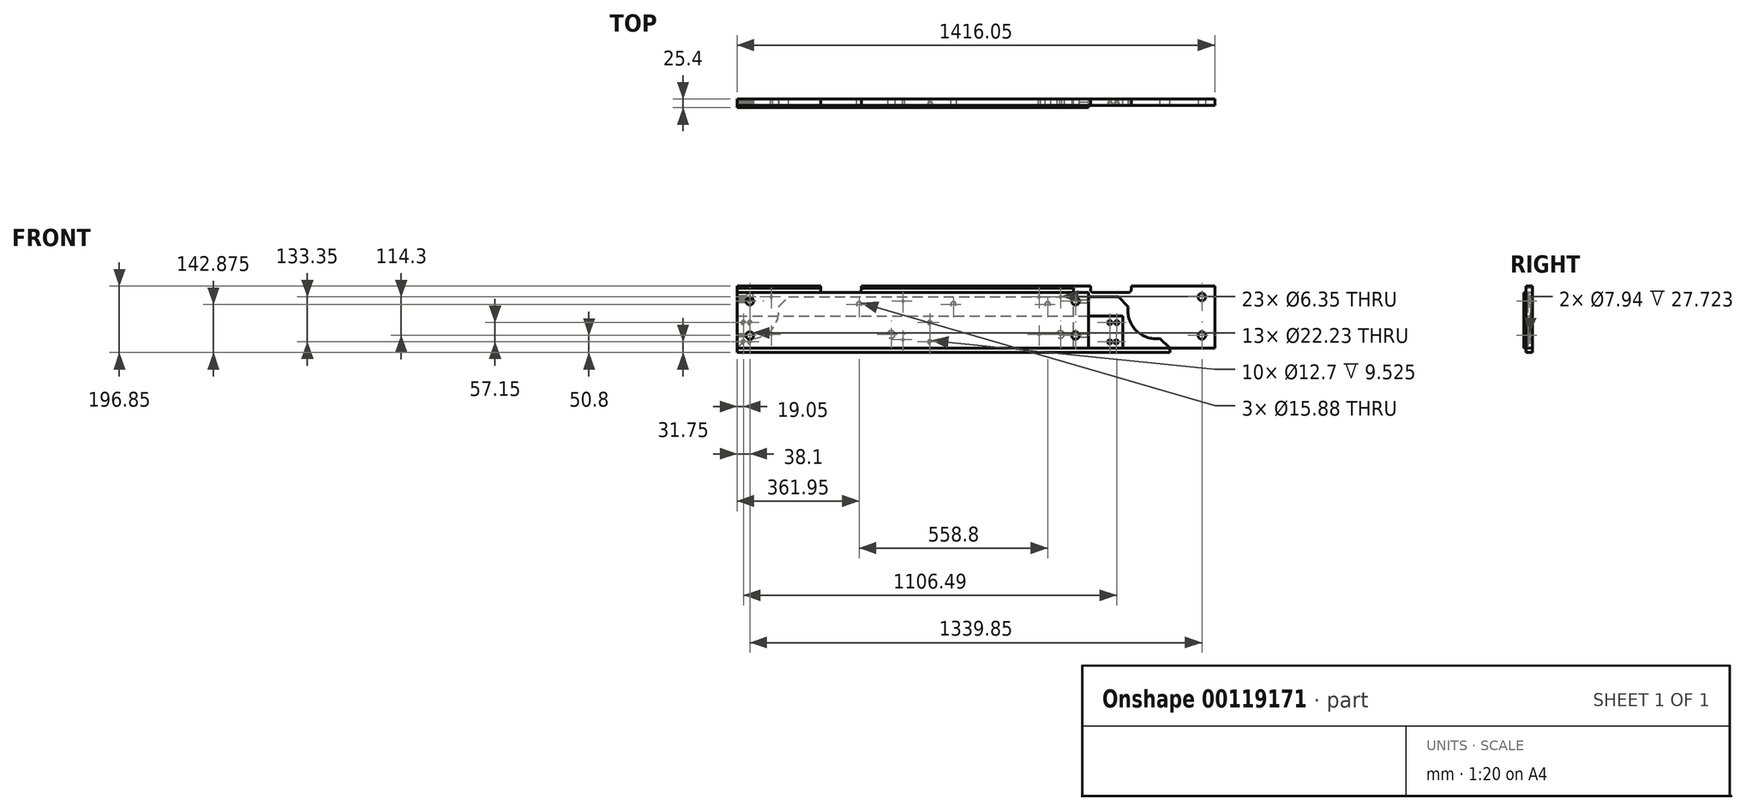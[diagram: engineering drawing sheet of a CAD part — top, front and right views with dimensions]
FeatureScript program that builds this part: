
annotation { "Feature Type Name" : "Feature", "Feature Type Description" : "" }
export const myFeature = defineFeature(function(context is Context, id is Id, definition is map)
    precondition{}
    {
        {
            var Q0;
            Q0=qCreatedBy(makeId("Front.planeOp"),FACE);
            var sketch = newSketch(context, id + "F30", { "sketchPlane" : qUnion([Q0])});
            skLineSegment(sketch, "E0.bottom", {"start": v(0, -12.7) * mm, "end": v(1282.7, -12.7) * mm});
            skLineSegment(sketch, "E0.top", {"start": v(152.4, 152.4) * mm, "end": v(1130.3, 152.4) * mm});
            skLineSegment(sketch, "E0.left", {"start": v(0, 0) * mm, "end": v(152.4, 152.4) * mm});
            skLineSegment(sketch, "E0.right", {"start": v(1282.7, 0) * mm, "end": v(1130.3, 152.4) * mm});
            skLineSegment(sketch, "E1", {"start": v(0, -12.7) * mm, "end": v(0, 0) * mm});
            skLineSegment(sketch, "E2", {"start": v(1282.7, -12.7) * mm, "end": v(1282.7, 0) * mm});
            skSolve(sketch);
        }
        {
            var Q0;
            Q0=makeQuery(id+"F30.imprint","IMPRINT",FACE,{"disambiguationData":[TD([[makeQuery(id+"F30.imprint","IMPRINT",EDGE,{"derivedFrom":sQuery(id+"F30.wireOp",EDGE,"E0.bottom")}),1.0]])]});
            extrude(context, id + "F31", {"entities" : qUnion([Q0]), "depth" : 19.05 * mm});
        }
        {
            var Q0;
            Q0=makeQuery(id+"F31.opExtrude","CAP_FACE",FACE,{"disambiguationData":[OSD([sQuery(id+"F30.wireOp",EDGE,"E0.bottom"),sQuery(id+"F30.wireOp",EDGE,"E0.top"),sQuery(id+"F30.wireOp",EDGE,"E0.left"),sQuery(id+"F30.wireOp",EDGE,"E0.right"),sQuery(id+"F30.wireOp",EDGE,"E1"),sQuery(id+"F30.wireOp",EDGE,"E2")])],"isStart":false});
            var sketch = newSketch(context, id + "F0", { "sketchPlane" : qUnion([Q0])});
            skCircle(sketch, "E3", {"center": v(1241.43, 111.13) * mm, "radius": 82.55 * mm});
            skCircle(sketch, "E4", {"center": v(41.28, 111.13) * mm, "radius": 82.55 * mm});
            skSolve(sketch);
        }
        {
            var Q0;
            {var subQ0=sQuery(id+"F0.wireOp",EDGE,"E4");var subQ1=makeQuery(id+"F31.opExtrude","CAP_EDGE",EDGE,{"disambiguationData":[OSD([sQuery(id+"F30.wireOp",EDGE,"E0.left")])],"isStart":false});var subQ2=makeQuery(id+"F0.imprint","INTERSECT",VERTEX,{"disambiguationData":[OD(0.0)],"derivedFrom":[subQ1,subQ0]});Q0=makeQuery(id+"F0.imprint","IMPRINT",FACE,{"disambiguationData":[TD([[makeQuery(id+"F0.imprint","IMPRINT",EDGE,{"disambiguationData":[TD([[subQ2,-1.0]])],"derivedFrom":subQ0}),1.0]])]});}
            var Q1;
            {var subQ0=sQuery(id+"F0.wireOp",EDGE,"E4");var subQ1=makeQuery(id+"F31.opExtrude","CAP_EDGE",EDGE,{"disambiguationData":[OSD([sQuery(id+"F30.wireOp",EDGE,"E0.left")])],"isStart":false});var subQ2=makeQuery(id+"F0.imprint","INTERSECT",VERTEX,{"disambiguationData":[OD(0.0)],"derivedFrom":[subQ1,subQ0]});Q1=makeQuery(id+"F0.imprint","IMPRINT",FACE,{"disambiguationData":[TD([[makeQuery(id+"F0.imprint","IMPRINT",EDGE,{"disambiguationData":[TD([[subQ2,1.0]])],"derivedFrom":subQ0}),1.0]])]});}
            var Q2;
            {var subQ0=sQuery(id+"F0.wireOp",EDGE,"E3");var subQ1=makeQuery(id+"F31.opExtrude","CAP_EDGE",EDGE,{"disambiguationData":[OSD([sQuery(id+"F30.wireOp",EDGE,"E0.right")])],"isStart":false});var subQ2=makeQuery(id+"F0.imprint","INTERSECT",VERTEX,{"disambiguationData":[OD(0.0)],"derivedFrom":[subQ1,subQ0]});Q2=makeQuery(id+"F0.imprint","IMPRINT",FACE,{"disambiguationData":[TD([[makeQuery(id+"F0.imprint","IMPRINT",EDGE,{"disambiguationData":[TD([[subQ2,1.0]])],"derivedFrom":subQ0}),1.0]])]});}
            var Q3;
            {var subQ0=sQuery(id+"F0.wireOp",EDGE,"E3");var subQ1=makeQuery(id+"F31.opExtrude","CAP_EDGE",EDGE,{"disambiguationData":[OSD([sQuery(id+"F30.wireOp",EDGE,"E0.right")])],"isStart":false});var subQ2=makeQuery(id+"F0.imprint","INTERSECT",VERTEX,{"disambiguationData":[OD(0.0)],"derivedFrom":[subQ1,subQ0]});Q3=makeQuery(id+"F0.imprint","IMPRINT",FACE,{"disambiguationData":[TD([[makeQuery(id+"F0.imprint","IMPRINT",EDGE,{"disambiguationData":[TD([[subQ2,-1.0]])],"derivedFrom":subQ0}),1.0]])]});}
            extrude(context, id + "F1", {"entities" : qUnion([Q0, Q1, Q2, Q3]), "operationType" : NewBodyOperationType.REMOVE, "oppositeDirection" : true, "depth" : 25.4 * mm});
        }
        {
            var Q0;
            Q0=makeQuery(id+"F31.opExtrude","CAP_FACE",FACE,{"disambiguationData":[OSD([sQuery(id+"F30.wireOp",EDGE,"E0.bottom"),sQuery(id+"F30.wireOp",EDGE,"E0.top"),sQuery(id+"F30.wireOp",EDGE,"E0.left"),sQuery(id+"F30.wireOp",EDGE,"E0.right"),sQuery(id+"F30.wireOp",EDGE,"E1"),sQuery(id+"F30.wireOp",EDGE,"E2")])],"isStart":false});
            var sketch = newSketch(context, id + "F2", { "sketchPlane" : qUnion([Q0])});
            skCircle(sketch, "E5", {"center": v(361.95, 130.18) * mm, "radius": 7.94 * mm});
            skCircle(sketch, "E6", {"center": v(641.35, 130.18) * mm, "radius": 7.94 * mm});
            skCircle(sketch, "E7", {"center": v(920.75, 130.18) * mm, "radius": 7.94 * mm});
            skSolve(sketch);
        }
        {
            var Q0;
            Q0 = qSketchRegion(id + "F2", true);
            extrude(context, id + "F3", {"entities" : qUnion([Q0]), "operationType" : NewBodyOperationType.REMOVE, "oppositeDirection" : true, "depth" : 50.8 * mm});
        }
        {
            var Q0;
            Q0=qCreatedBy(makeId("Front.planeOp"),FACE);
            var sketch = newSketch(context, id + "F4", { "sketchPlane" : qUnion([Q0])});
            skLineSegment(sketch, "E8.bottom", {"start": v(0, 0) * mm, "end": v(996.95, 0) * mm});
            skLineSegment(sketch, "E8.top", {"start": v(0, 177.8) * mm, "end": v(996.95, 177.8) * mm});
            skLineSegment(sketch, "E8.left", {"start": v(0, 0) * mm, "end": v(0, 177.8) * mm});
            skLineSegment(sketch, "E8.right", {"start": v(996.95, 0) * mm, "end": v(996.95, 177.8) * mm});
            skSolve(sketch);
        }
        {
            var Q0;
            Q0=makeQuery(id+"F4.imprint","IMPRINT",FACE,{"disambiguationData":[TD([[makeQuery(id+"F4.imprint","IMPRINT",EDGE,{"derivedFrom":sQuery(id+"F4.wireOp",EDGE,"E8.bottom")}),1.0]])]});
            extrude(context, id + "F5", {"entities" : qUnion([Q0]), "depth" : 19.05 * mm});
        }
        {
            var Q0;
            Q0=makeQuery(id+"F5.opExtrude","CAP_FACE",FACE,{"disambiguationData":[OSD([sQuery(id+"F4.wireOp",EDGE,"E8.bottom"),sQuery(id+"F4.wireOp",EDGE,"E8.top"),sQuery(id+"F4.wireOp",EDGE,"E8.left"),sQuery(id+"F4.wireOp",EDGE,"E8.right")])],"isStart":false});
            var sketch = newSketch(context, id + "F6", { "sketchPlane" : qUnion([Q0])});
            skCircle(sketch, "E9", {"center": v(958.85, 152.4) * mm, "radius": 3.18 * mm});
            skCircle(sketch, "E10", {"center": v(958.85, 41.27) * mm, "radius": 3.18 * mm});
            skCircle(sketch, "E11", {"center": v(492.13, 139.7) * mm, "radius": 3.18 * mm});
            skCircle(sketch, "E12", {"center": v(492.13, 25.4) * mm, "radius": 3.18 * mm});
            skCircle(sketch, "E13", {"center": v(38.1, 152.4) * mm, "radius": 3.18 * mm});
            skCircle(sketch, "E14", {"center": v(38.1, 41.27) * mm, "radius": 3.18 * mm});
            skCircle(sketch, "E15", {"center": v(101.6, 152.4) * mm, "radius": 3.18 * mm});
            skCircle(sketch, "E16", {"center": v(101.6, 41.27) * mm, "radius": 3.18 * mm});
            skCircle(sketch, "E17", {"center": v(895.35, 152.4) * mm, "radius": 3.18 * mm});
            skCircle(sketch, "E18", {"center": v(895.35, 41.27) * mm, "radius": 3.18 * mm});
            skSolve(sketch);
        }
        {
            var Q0;
            Q0 = qSketchRegion(id + "F6", true);
            extrude(context, id + "F7", {"entities" : qUnion([Q0]), "operationType" : NewBodyOperationType.REMOVE, "oppositeDirection" : true, "depth" : 25.4 * mm});
        }
        {
            var Q0;
            Q0=qCreatedBy(makeId("Front.planeOp"),FACE);
            var sketch = newSketch(context, id + "F8", { "sketchPlane" : qUnion([Q0])});
            skLineSegment(sketch, "E19.bottom", {"start": v(0, 0) * mm, "end": v(1041.4, 0) * mm});
            skLineSegment(sketch, "E19.top", {"start": v(0, 165.1) * mm, "end": v(1041.4, 165.1) * mm});
            skLineSegment(sketch, "E19.left", {"start": v(0, 0) * mm, "end": v(0, 165.1) * mm});
            skLineSegment(sketch, "E19.right", {"start": v(1041.4, 0) * mm, "end": v(1041.4, 165.1) * mm});
            skSolve(sketch);
        }
        {
            var Q0;
            Q0=makeQuery(id+"F8.imprint","IMPRINT",FACE,{"disambiguationData":[TD([[makeQuery(id+"F8.imprint","IMPRINT",EDGE,{"derivedFrom":sQuery(id+"F8.wireOp",EDGE,"E19.bottom")}),1.0]])]});
            extrude(context, id + "F9", {"entities" : qUnion([Q0]), "depth" : 25.4 * mm});
        }
        {
            var Q0;
            Q0=makeQuery(id+"F9.opExtrude","CAP_FACE",FACE,{"disambiguationData":[OSD([sQuery(id+"F8.wireOp",EDGE,"E19.bottom"),sQuery(id+"F8.wireOp",EDGE,"E19.top"),sQuery(id+"F8.wireOp",EDGE,"E19.left"),sQuery(id+"F8.wireOp",EDGE,"E19.right")])],"isStart":false});
            var sketch = newSketch(context, id + "F10", { "sketchPlane" : qUnion([Q0])});
            skCircle(sketch, "E20", {"center": v(1003.3, 139.7) * mm, "radius": 11.11 * mm});
            skCircle(sketch, "E21", {"center": v(1003.3, 38.1) * mm, "radius": 11.11 * mm});
            skSolve(sketch);
        }
        {
            var Q0;
            Q0 = qSketchRegion(id + "F10", true);
            extrude(context, id + "F11", {"entities" : qUnion([Q0]), "operationType" : NewBodyOperationType.REMOVE, "oppositeDirection" : true, "depth" : 25.4 * mm});
        }
        {
            var Q0;
            Q0=makeQuery(id+"F9.opExtrude","SWEPT_FACE",FACE,{"disambiguationData":[OSD([sQuery(id+"F8.wireOp",EDGE,"E19.right")])]});
            var sketch = newSketch(context, id + "F12", { "sketchPlane" : qUnion([Q0])});
            skCircle(sketch, "E22", {"center": v(-12.7, 38.1) * mm, "radius": 3.97 * mm});
            skCircle(sketch, "E23", {"center": v(-12.7, 139.7) * mm, "radius": 3.97 * mm});
            skSolve(sketch);
        }
        {
            var Q0;
            Q0 = qSketchRegion(id + "F12", true);
            extrude(context, id + "F13", {"entities" : qUnion([Q0]), "operationType" : NewBodyOperationType.REMOVE, "oppositeDirection" : true, "depth" : 38.1 * mm});
        }
        {
            var Q0;
            Q0=makeQuery(id+"F9.opExtrude","CAP_FACE",FACE,{"disambiguationData":[OSD([sQuery(id+"F8.wireOp",EDGE,"E19.bottom"),sQuery(id+"F8.wireOp",EDGE,"E19.top"),sQuery(id+"F8.wireOp",EDGE,"E19.left"),sQuery(id+"F8.wireOp",EDGE,"E19.right")])],"isStart":false});
            var sketch = newSketch(context, id + "F14", { "sketchPlane" : qUnion([Q0])});
            skCircle(sketch, "E24", {"center": v(38.1, 139.7) * mm, "radius": 11.11 * mm});
            skCircle(sketch, "E25", {"center": v(38.1, 38.1) * mm, "radius": 11.11 * mm});
            skSolve(sketch);
        }
        {
            var Q0;
            Q0 = qSketchRegion(id + "F14", true);
            extrude(context, id + "F15", {"entities" : qUnion([Q0]), "operationType" : NewBodyOperationType.REMOVE, "oppositeDirection" : true, "depth" : 25.4 * mm});
        }
        {
            var Q0;
            Q0=makeQuery(id+"F9.opExtrude","SWEPT_FACE",FACE,{"disambiguationData":[OSD([sQuery(id+"F8.wireOp",EDGE,"E19.left")])]});
            var sketch = newSketch(context, id + "F16", { "sketchPlane" : qUnion([Q0])});
            skCircle(sketch, "E26", {"center": v(12.7, 139.7) * mm, "radius": 3.97 * mm});
            skCircle(sketch, "E27", {"center": v(12.7, 38.1) * mm, "radius": 3.97 * mm});
            skSolve(sketch);
        }
        {
            var Q0;
            Q0 = qSketchRegion(id + "F16", true);
            extrude(context, id + "F17", {"entities" : qUnion([Q0]), "operationType" : NewBodyOperationType.REMOVE, "oppositeDirection" : true, "depth" : 38.1 * mm});
        }
        {
            var Q0;
            Q0=qCreatedBy(makeId("Front.planeOp"),FACE);
            var sketch = newSketch(context, id + "F18", { "sketchPlane" : qUnion([Q0])});
            skLineSegment(sketch, "E28.bottom", {"start": v(0, 0) * mm, "end": v(1143, 0) * mm});
            skLineSegment(sketch, "E28.top", {"start": v(0, 95.25) * mm, "end": v(1143, 95.25) * mm});
            skLineSegment(sketch, "E28.left", {"start": v(0, 0) * mm, "end": v(0, 95.25) * mm});
            skLineSegment(sketch, "E28.right", {"start": v(1143, 0) * mm, "end": v(1143, 95.25) * mm});
            skSolve(sketch);
        }
        {
            var Q0;
            Q0=makeQuery(id+"F18.imprint","IMPRINT",FACE,{"disambiguationData":[TD([[makeQuery(id+"F18.imprint","IMPRINT",EDGE,{"derivedFrom":sQuery(id+"F18.wireOp",EDGE,"E28.bottom")}),1.0]])]});
            extrude(context, id + "F19", {"entities" : qUnion([Q0]), "depth" : 19.05 * mm});
        }
        {
            var Q0;
            Q0=makeQuery(id+"F19.opExtrude","CAP_FACE",FACE,{"disambiguationData":[OSD([sQuery(id+"F18.wireOp",EDGE,"E28.bottom"),sQuery(id+"F18.wireOp",EDGE,"E28.top"),sQuery(id+"F18.wireOp",EDGE,"E28.left"),sQuery(id+"F18.wireOp",EDGE,"E28.right")])],"isStart":false});
            var sketch = newSketch(context, id + "F20", { "sketchPlane" : qUnion([Q0])});
            skPoint(sketch, "E29", {"position": v(19.05, 76.2) * mm});
            skPoint(sketch, "E30", {"position": v(38.1, 76.2) * mm});
            skPoint(sketch, "E31", {"position": v(19.05, 19.05) * mm});
            skPoint(sketch, "E32", {"position": v(38.1, 19.05) * mm});
            skPoint(sketch, "E33", {"position": v(571.5, 76.2) * mm});
            skPoint(sketch, "E34", {"position": v(571.5, 19.05) * mm});
            skPoint(sketch, "E35", {"position": v(1104.9, 19.05) * mm});
            skPoint(sketch, "E36", {"position": v(1123.95, 19.05) * mm});
            skPoint(sketch, "E37", {"position": v(1125.54, 76.2) * mm});
            skPoint(sketch, "E38", {"position": v(1104.9, 76.2) * mm});
            skSolve(sketch);
        }
        {
            var Q0;
            Q0=sQuery(id+"F20.wireOp",VERTEX,"E29");
            var Q1;
            Q1=sQuery(id+"F20.wireOp",VERTEX,"E30");
            var Q2;
            Q2=sQuery(id+"F20.wireOp",VERTEX,"E31");
            var Q3;
            Q3=sQuery(id+"F20.wireOp",VERTEX,"E32");
            var Q4;
            Q4=sQuery(id+"F20.wireOp",VERTEX,"E33");
            var Q5;
            Q5=sQuery(id+"F20.wireOp",VERTEX,"E34");
            var Q6;
            Q6=sQuery(id+"F20.wireOp",VERTEX,"E38");
            var Q7;
            Q7=sQuery(id+"F20.wireOp",VERTEX,"E37");
            var Q8;
            Q8=sQuery(id+"F20.wireOp",VERTEX,"E35");
            var Q9;
            Q9=sQuery(id+"F20.wireOp",VERTEX,"E36");
            var Q10;
            Q10=makeQuery(id+"F19.opExtrude","SWEPT_BODY",BODY,{"disambiguationData":[OSD([sQuery(id+"F18.wireOp",EDGE,"E28.bottom"),sQuery(id+"F18.wireOp",EDGE,"E28.top"),sQuery(id+"F18.wireOp",EDGE,"E28.left"),sQuery(id+"F18.wireOp",EDGE,"E28.right")])]});
            hole(context, id + "F21", {"style" : HoleStyle.C_BORE, "endStyle" : HoleEndStyle.THROUGH, "holeDiameter" : 6.35 * mm, "cBoreDiameter" : 12.7 * mm, "cBoreDepth" : 9.52 * mm, "isTappedThrough" : true, "tappedDepth" : 12.7 * mm, "tapClearance" : 3, "locations" : qUnion([Q0, Q1, Q2, Q3, Q4, Q5, Q6, Q7, Q8, Q9]), "scope" : qUnion([Q10])});
        }
        {
            var Q0;
            Q0=qCreatedBy(makeId("Front.planeOp"),FACE);
            var sketch = newSketch(context, id + "F22", { "sketchPlane" : qUnion([Q0])});
            skLineSegment(sketch, "E39.bottom", {"start": v(0, 0) * mm, "end": v(1416.05, 0) * mm});
            skLineSegment(sketch, "E39.top", {"start": v(0, 184.15) * mm, "end": v(1416.05, 184.15) * mm});
            skLineSegment(sketch, "E39.left", {"start": v(0, 0) * mm, "end": v(0, 184.15) * mm});
            skLineSegment(sketch, "E39.right", {"start": v(1416.05, 0) * mm, "end": v(1416.05, 184.15) * mm});
            skSolve(sketch);
        }
        {
            var Q0;
            Q0=makeQuery(id+"F22.imprint","IMPRINT",FACE,{"disambiguationData":[TD([[makeQuery(id+"F22.imprint","IMPRINT",EDGE,{"derivedFrom":sQuery(id+"F22.wireOp",EDGE,"E39.bottom")}),1.0]])]});
            extrude(context, id + "F23", {"entities" : qUnion([Q0]), "depth" : 19.05 * mm});
        }
        {
            var Q0;
            Q0=makeQuery(id+"F23.opExtrude","CAP_FACE",FACE,{"disambiguationData":[OSD([sQuery(id+"F22.wireOp",EDGE,"E39.bottom"),sQuery(id+"F22.wireOp",EDGE,"E39.top"),sQuery(id+"F22.wireOp",EDGE,"E39.left"),sQuery(id+"F22.wireOp",EDGE,"E39.right")])],"isStart":false});
            var sketch = newSketch(context, id + "F24", { "sketchPlane" : qUnion([Q0])});
            skPoint(sketch, "E40", {"position": v(38.1, 38.1) * mm});
            skPoint(sketch, "E41", {"position": v(38.1, 152.4) * mm});
            skPoint(sketch, "E42", {"position": v(1377.95, 152.4) * mm});
            skPoint(sketch, "E43", {"position": v(1377.95, 38.1) * mm});
            skPoint(sketch, "E44", {"position": v(958.85, 41.28) * mm});
            skPoint(sketch, "E45", {"position": v(457.2, 41.28) * mm});
            skLineSegment(sketch, "E46.bottom", {"start": v(247.65, 184.15) * mm, "end": v(368.3, 184.15) * mm});
            skLineSegment(sketch, "E46.top", {"start": v(247.65, 165.1) * mm, "end": v(368.3, 165.1) * mm});
            skLineSegment(sketch, "E46.left", {"start": v(247.65, 184.15) * mm, "end": v(247.65, 165.1) * mm});
            skLineSegment(sketch, "E46.right", {"start": v(368.3, 184.15) * mm, "end": v(368.3, 165.1) * mm});
            skLineSegment(sketch, "E47.bottom", {"start": v(1047.75, 184.15) * mm, "end": v(1168.4, 184.15) * mm});
            skLineSegment(sketch, "E47.top", {"start": v(1047.75, 165.1) * mm, "end": v(1168.4, 165.1) * mm});
            skLineSegment(sketch, "E47.left", {"start": v(1047.75, 184.15) * mm, "end": v(1047.75, 165.1) * mm});
            skLineSegment(sketch, "E47.right", {"start": v(1168.4, 184.15) * mm, "end": v(1168.4, 165.1) * mm});
            skSolve(sketch);
        }
        {
            var Q0;
            Q0=makeQuery(id+"F24.imprint","IMPRINT",FACE,{"disambiguationData":[TD([[makeQuery(id+"F24.imprint","IMPRINT",EDGE,{"derivedFrom":sQuery(id+"F24.wireOp",EDGE,"E46.bottom")}),-1.0]])]});
            var Q1;
            Q1=makeQuery(id+"F24.imprint","IMPRINT",FACE,{"disambiguationData":[TD([[makeQuery(id+"F24.imprint","IMPRINT",EDGE,{"derivedFrom":sQuery(id+"F24.wireOp",EDGE,"E47.bottom")}),-1.0]])]});
            extrude(context, id + "F25", {"entities" : qUnion([Q0, Q1]), "operationType" : NewBodyOperationType.REMOVE, "oppositeDirection" : true, "depth" : 25.4 * mm});
        }
        {
            var Q0;
            Q0=sQuery(id+"F24.wireOp",VERTEX,"E41");
            var Q1;
            Q1=sQuery(id+"F24.wireOp",VERTEX,"E40");
            var Q2;
            Q2=sQuery(id+"F24.wireOp",VERTEX,"E42");
            var Q3;
            Q3=sQuery(id+"F24.wireOp",VERTEX,"E43");
            var Q4;
            Q4=sQuery(id+"F24.wireOp",VERTEX,"E45");
            var Q5;
            Q5=sQuery(id+"F24.wireOp",VERTEX,"E44");
            var Q6;
            Q6=makeQuery(id+"F23.opExtrude","SWEPT_BODY",BODY,{"disambiguationData":[OSD([sQuery(id+"F22.wireOp",EDGE,"E39.bottom"),sQuery(id+"F22.wireOp",EDGE,"E39.top"),sQuery(id+"F22.wireOp",EDGE,"E39.left"),sQuery(id+"F22.wireOp",EDGE,"E39.right")])]});
            hole(context, id + "F26", {"style" : HoleStyle.SIMPLE, "endStyle" : HoleEndStyle.THROUGH, "holeDiameter" : 22.22 * mm, "isTappedThrough" : true, "tappedDepth" : 12.7 * mm, "tapClearance" : 3, "locations" : qUnion([Q0, Q1, Q2, Q3, Q4, Q5]), "scope" : qUnion([Q6])});
        }
        {
            var Q0;
            Q0=makeQuery(id+"F23.opExtrude","SWEPT_FACE",FACE,{"disambiguationData":[OSD([sQuery(id+"F22.wireOp",EDGE,"E39.left")])]});
            var sketch = newSketch(context, id + "F27", { "sketchPlane" : qUnion([Q0])});
            skPoint(sketch, "E48", {"position": v(9.53, 152.4) * mm});
            skPoint(sketch, "E49", {"position": v(9.53, 38.1) * mm});
            skSolve(sketch);
        }
        {
            var Q0;
            Q0=sQuery(id+"F27.wireOp",VERTEX,"E48");
            var Q1;
            Q1=sQuery(id+"F27.wireOp",VERTEX,"E49");
            var Q2;
            Q2=makeQuery(id+"F23.opExtrude","SWEPT_BODY",BODY,{"disambiguationData":[OSD([sQuery(id+"F22.wireOp",EDGE,"E39.bottom"),sQuery(id+"F22.wireOp",EDGE,"E39.top"),sQuery(id+"F22.wireOp",EDGE,"E39.left"),sQuery(id+"F22.wireOp",EDGE,"E39.right")])]});
            hole(context, id + "F28", {"style" : HoleStyle.SIMPLE, "endStyle" : HoleEndStyle.BLIND, "holeDiameter" : 6.35 * mm, "holeDepth" : 38.1 * mm, "isTappedThrough" : true, "tappedDepth" : 12.7 * mm, "tapClearance" : 3, "locations" : qUnion([Q0, Q1]), "scope" : qUnion([Q2])});
        }
        {
            var Q0;
            Q0=makeQuery(id+"F25.boolean.opBoolean","COPY",EDGE,{"derivedFrom":makeQuery(id+"F25.opExtrude","SWEPT_EDGE",EDGE,{"disambiguationData":[OSD([sQuery(id+"F24.wireOp",EDGE,"E46.top"),sQuery(id+"F24.wireOp",EDGE,"E46.right")])]})});
            var Q1;
            Q1=makeQuery(id+"F25.boolean.opBoolean","COPY",EDGE,{"derivedFrom":makeQuery(id+"F25.opExtrude","SWEPT_EDGE",EDGE,{"disambiguationData":[OSD([sQuery(id+"F24.wireOp",EDGE,"E46.top"),sQuery(id+"F24.wireOp",EDGE,"E46.left")])]})});
            var Q2;
            Q2=makeQuery(id+"F25.boolean.opBoolean","COPY",EDGE,{"derivedFrom":makeQuery(id+"F25.opExtrude","SWEPT_EDGE",EDGE,{"disambiguationData":[OSD([sQuery(id+"F24.wireOp",EDGE,"E47.top"),sQuery(id+"F24.wireOp",EDGE,"E47.right")])]})});
            var Q3;
            Q3=makeQuery(id+"F25.boolean.opBoolean","COPY",EDGE,{"derivedFrom":makeQuery(id+"F25.opExtrude","SWEPT_EDGE",EDGE,{"disambiguationData":[OSD([sQuery(id+"F24.wireOp",EDGE,"E47.top"),sQuery(id+"F24.wireOp",EDGE,"E47.left")])]})});
            fillet(context, id + "F29", {"entities" : qUnion([Q0, Q1, Q2, Q3]), "radius" : 9.52 * mm, "tangentPropagation" : true, "allowEdgeOverflow" : false});
        }
    });
